# Revit family: 63_UN_Downlighter_Thunder Series 14-28W D232_Natec
name_source: partatom
category: Lighting Fixtures
units: mm (PartAtom-declared; Revit-internal decimal feet)

## family parameters
Always vertical = Yes
Cut with Voids When Loaded = Yes
Light Source = Yes
OmniClass Number = 23.80.70.11.14.11
OmniClass Title = Downlights
Part Type = Normal
Room Calculation Point = Yes
Round Connector Dimension = Use Diameter
Shared = No
Work Plane-Based = No

## types (4) — shared parameters
Assembly Code = 63.0
Color Filter = 16777215
Dimming Lamp Color Temperature Shift = <None>
Housing_Material = Laminate, White
IfcExportAs = IfcLightFixtureType
IfcExportType = USERDEFINED
Lamp = LED
Manufacturer = Natec Lighting
Model = Downlighter
Tilt Angle = 90.00°
Type Comments = Thunder series D232
URL = https://nateclighting.nl
Voltage = 230 V

## per-type parameters (varying)
| type | Apparent Load | Luminous Flux (lm) | Photometric Web File | Wattage Comments |
| Thunder 14W 3000K (Tri-white) 110lmw | 14 VA | 3312 lm | Thunder 14W 3000K (Tri-white) 110lmw.IES | 14W |
| Thunder 28W 3000K (Tri-white) 110lmw | 28 VA | 3312 lm | Thunder 28W 3000K (Tri-white) 110lmw.IES | 28W |
| Thunder 28W 4000K (Tri-white) 110lmw | 28 VA | 3169 lm | Thunder 28W 4000K (Tri-white) 110lmw.IES | 28W |
| Thunder 28W 5700K (Tri-white) 110lmw | 28 VA | 3398 lm | Thunder 28W 5700K (Tri-white) 110lmw.IES | 28W |

## geometry (parser evidence)
native form markers: Sweep x3
no freeform markers — native parametric forms only
